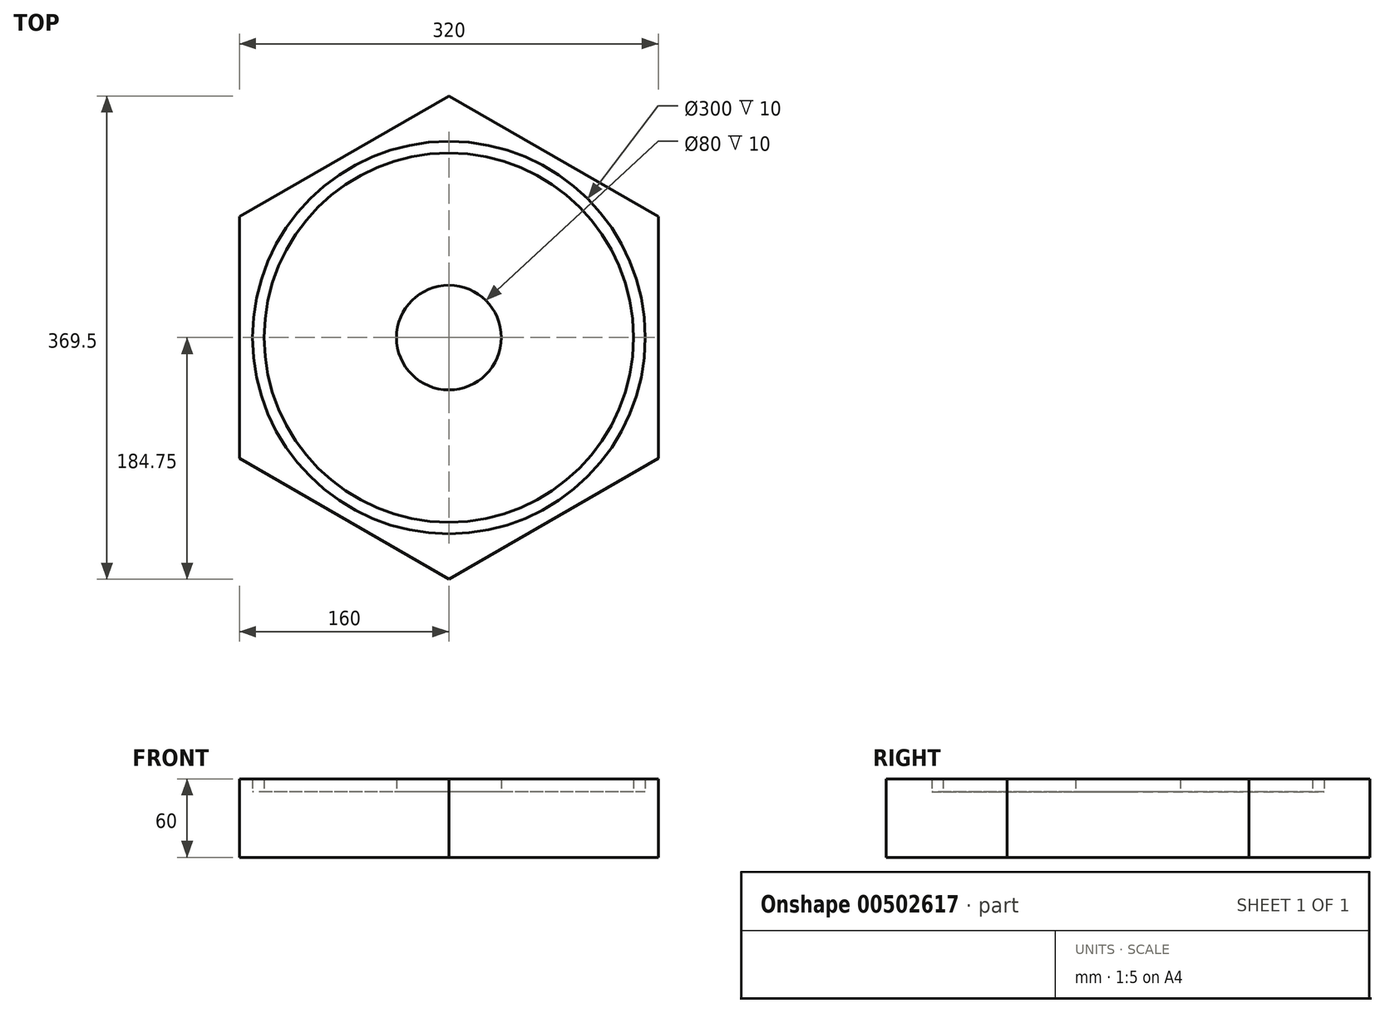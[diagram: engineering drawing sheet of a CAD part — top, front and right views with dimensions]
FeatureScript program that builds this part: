
annotation { "Feature Type Name" : "Feature", "Feature Type Description" : "" }
export const myFeature = defineFeature(function(context is Context, id is Id, definition is map)
    precondition{}
    {
        {
            var Q0;
            Q0=qCreatedBy(makeId("Top.planeOp"),FACE);
            var sketch = newSketch(context, id + "F0", { "sketchPlane" : qUnion([Q0])});
            skCircle(sketch, "E0.cCircle", {"center": v(0, 0) * mm, "radius": 160 * mm, "construction": true});
            skLineSegment(sketch, "E0.0", {"start": v(160, 92.38) * mm, "end": v(160, -92.38) * mm});
            skLineSegment(sketch, "E0.1", {"start": v(160, -92.38) * mm, "end": v(0, -184.75) * mm});
            skLineSegment(sketch, "E0.2", {"start": v(0, -184.75) * mm, "end": v(-160, -92.38) * mm});
            skLineSegment(sketch, "E0.3", {"start": v(-160, -92.38) * mm, "end": v(-160, 92.38) * mm});
            skLineSegment(sketch, "E0.4", {"start": v(-160, 92.38) * mm, "end": v(0, 184.75) * mm});
            skLineSegment(sketch, "E0.5", {"start": v(0, 184.75) * mm, "end": v(160, 92.38) * mm});
            skPoint(sketch, "E0.0.midPoint", {"position": v(160, 0) * mm});
            skSolve(sketch);
        }
        {
            var Q0;
            Q0 = qSketchRegion(id + "F0", true);
            extrude(context, id + "F1", {"entities" : qUnion([Q0]), "depth" : 50 * mm});
        }
        {
            var Q0;
            Q0=makeQuery(id+"F1.opExtrude","CAP_FACE",FACE,{"disambiguationData":[OSD([sQuery(id+"F0.wireOp",EDGE,"E0.0"),sQuery(id+"F0.wireOp",EDGE,"E0.1"),sQuery(id+"F0.wireOp",EDGE,"E0.2"),sQuery(id+"F0.wireOp",EDGE,"E0.3"),sQuery(id+"F0.wireOp",EDGE,"E0.4"),sQuery(id+"F0.wireOp",EDGE,"E0.5")])],"isStart":false});
            var sketch = newSketch(context, id + "F2", { "sketchPlane" : qUnion([Q0])});
            skCircle(sketch, "E1", {"center": v(0, 0) * mm, "radius": 150 * mm});
            skSolve(sketch);
        }
        {
            var Q0;
            Q0=makeQuery(id+"F2.imprint","IMPRINT",FACE,{"disambiguationData":[TD([[makeQuery(id+"F2.imprint","IMPRINT",EDGE,{"derivedFrom":sQuery(id+"F2.wireOp",EDGE,"E1")}),-1.0]])]});
            var sketch = newSketch(context, id + "F3", { "sketchPlane" : qUnion([Q0])});
            skCircle(sketch, "E2", {"center": v(0, 0) * mm, "radius": 141.12 * mm});
            skCircle(sketch, "E3", {"center": v(0, 0) * mm, "radius": 40 * mm});
            skSolve(sketch);
        }
        {
            var Q0;
            Q0=makeQuery(id+"F3.imprint","IMPRINT",FACE,{"disambiguationData":[TD([[makeQuery(id+"F3.imprint","IMPRINT",EDGE,{"derivedFrom":makeQuery(id+"F2.imprint","IMPRINT",EDGE,{"derivedFrom":sQuery(id+"F2.wireOp",EDGE,"E1")})}),-1.0]])]});
            extrude(context, id + "F4", {"entities" : qUnion([Q0]), "operationType" : NewBodyOperationType.ADD, "depth" : 10 * mm});
        }
        {
            var Q0;
            Q0 = qSketchRegion(id + "F3", true);
            extrude(context, id + "F5", {"entities" : qUnion([Q0]), "operationType" : NewBodyOperationType.ADD, "depth" : 10 * mm});
        }
    });
